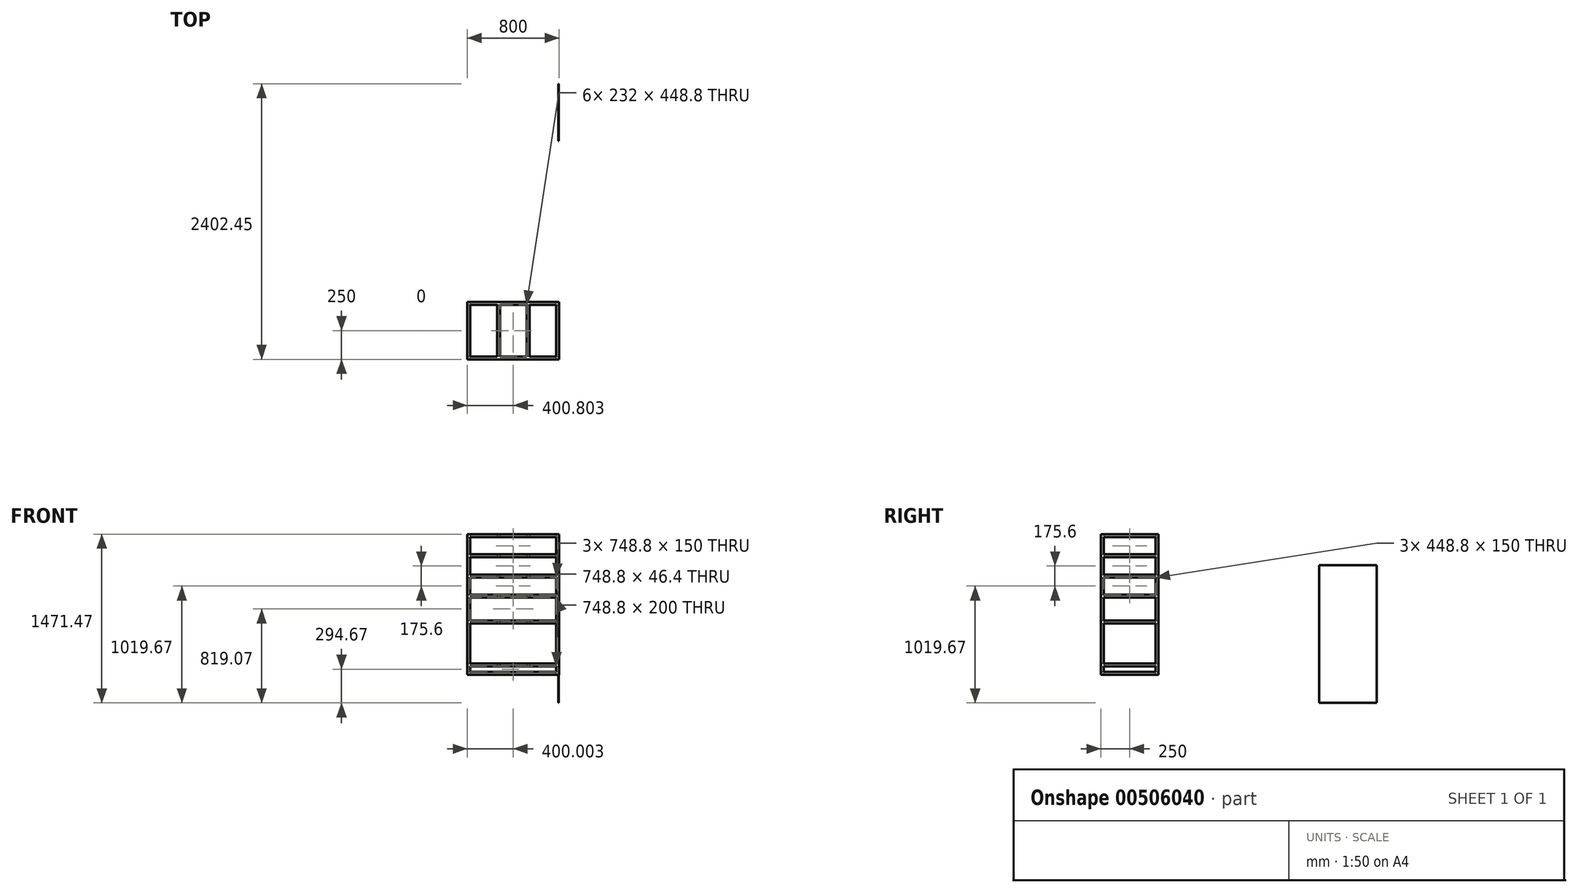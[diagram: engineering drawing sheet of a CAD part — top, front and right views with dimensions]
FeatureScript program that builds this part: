
annotation { "Feature Type Name" : "Feature", "Feature Type Description" : "" }
export const myFeature = defineFeature(function(context is Context, id is Id, definition is map)
    precondition{}
    {
        {
            var Q0;
            Q0=qCreatedBy(makeId("Top.planeOp"),FACE);
            var sketch = newSketch(context, id + "F0", { "sketchPlane" : qUnion([Q0])});
            skLineSegment(sketch, "E0.bottom", {"start": v(-792, -474.11) * mm, "end": v(8, -474.11) * mm});
            skLineSegment(sketch, "E0.top", {"start": v(-792, 25.89) * mm, "end": v(8, 25.89) * mm});
            skLineSegment(sketch, "E0.left", {"start": v(-792, -474.11) * mm, "end": v(-792, 25.89) * mm});
            skLineSegment(sketch, "E0.right", {"start": v(8, -474.11) * mm, "end": v(8, 25.89) * mm});
            skLineSegment(sketch, "E1.0", {"start": v(-766.4, -448.51) * mm, "end": v(-766.4, 0.29) * mm});
            skLineSegment(sketch, "E1.1", {"start": v(-766.4, -448.51) * mm, "end": v(-17.6, -448.51) * mm});
            skLineSegment(sketch, "E1.2", {"start": v(-17.6, -448.51) * mm, "end": v(-17.6, 0.29) * mm});
            skLineSegment(sketch, "E1.3", {"start": v(-766.4, 0.29) * mm, "end": v(-17.6, 0.29) * mm});
            skSolve(sketch);
        }
        {
            var Q0;
            Q0=makeQuery(id+"F0.imprint","IMPRINT",FACE,{"disambiguationData":[TD([[makeQuery(id+"F0.imprint","IMPRINT",EDGE,{"derivedFrom":sQuery(id+"F0.wireOp",EDGE,"E0.bottom")}),1.0]])]});
            extrude(context, id + "F1", {"entities" : qUnion([Q0]), "depth" : 25.6 * mm});
        }
        {
            var Q0;
            Q0=makeQuery(id+"F1.opExtrude","CAP_FACE",FACE,{"disambiguationData":[OSD([sQuery(id+"F0.wireOp",EDGE,"E0.bottom"),sQuery(id+"F0.wireOp",EDGE,"E0.top"),sQuery(id+"F0.wireOp",EDGE,"E0.left"),sQuery(id+"F0.wireOp",EDGE,"E0.right"),sQuery(id+"F0.wireOp",EDGE,"E1.0"),sQuery(id+"F0.wireOp",EDGE,"E1.1"),sQuery(id+"F0.wireOp",EDGE,"E1.2"),sQuery(id+"F0.wireOp",EDGE,"E1.3")])],"isStart":true});
            var sketch = newSketch(context, id + "F2", { "sketchPlane" : qUnion([Q0])});
            skLineSegment(sketch, "E2.bottom", {"start": v(-792, 474.11) * mm, "end": v(-766.4, 474.11) * mm});
            skLineSegment(sketch, "E2.top", {"start": v(-792, 448.51) * mm, "end": v(-766.4, 448.51) * mm});
            skLineSegment(sketch, "E2.left", {"start": v(-792, 474.11) * mm, "end": v(-792, 448.51) * mm});
            skLineSegment(sketch, "E2.right", {"start": v(-766.4, 474.11) * mm, "end": v(-766.4, 448.51) * mm});
            skLineSegment(sketch, "E3.bottom", {"start": v(8, 474.11) * mm, "end": v(-17.6, 474.11) * mm});
            skLineSegment(sketch, "E3.top", {"start": v(8, 448.51) * mm, "end": v(-17.6, 448.51) * mm});
            skLineSegment(sketch, "E3.left", {"start": v(8, 474.11) * mm, "end": v(8, 448.51) * mm});
            skLineSegment(sketch, "E3.right", {"start": v(-17.6, 474.11) * mm, "end": v(-17.6, 448.51) * mm});
            skLineSegment(sketch, "E4.bottom", {"start": v(8, -25.89) * mm, "end": v(-17.6, -25.89) * mm});
            skLineSegment(sketch, "E4.top", {"start": v(8, -0.29) * mm, "end": v(-17.6, -0.29) * mm});
            skLineSegment(sketch, "E4.left", {"start": v(8, -25.89) * mm, "end": v(8, -0.29) * mm});
            skLineSegment(sketch, "E4.right", {"start": v(-17.6, -25.89) * mm, "end": v(-17.6, -0.29) * mm});
            skLineSegment(sketch, "E5.bottom", {"start": v(-792, -25.89) * mm, "end": v(-766.4, -25.89) * mm});
            skLineSegment(sketch, "E5.top", {"start": v(-792, -0.29) * mm, "end": v(-766.4, -0.29) * mm});
            skLineSegment(sketch, "E5.left", {"start": v(-792, -25.89) * mm, "end": v(-792, -0.29) * mm});
            skLineSegment(sketch, "E5.right", {"start": v(-766.4, -25.89) * mm, "end": v(-766.4, -0.29) * mm});
            skSolve(sketch);
        }
        {
            var Q0;
            Q0 = qSketchRegion(id + "F2", true);
            extrude(context, id + "F3", {"entities" : qUnion([Q0]), "operationType" : NewBodyOperationType.ADD, "depth" : (1200) * mm});
        }
        {
            var Q0;
            Q0=makeQuery(id+"F3.opExtrude","SWEPT_FACE",FACE,{"disambiguationData":[OSD([sQuery(id+"F2.wireOp",EDGE,"E2.right")])]});
            var sketch = newSketch(context, id + "F4", { "sketchPlane" : qUnion([Q0])});
            skLineSegment(sketch, "E6.bottom", {"start": v(-474.11, -150) * mm, "end": v(-448.51, -150) * mm});
            skLineSegment(sketch, "E6.top", {"start": v(-474.11, -175.6) * mm, "end": v(-448.51, -175.6) * mm});
            skLineSegment(sketch, "E6.left", {"start": v(-474.11, -150) * mm, "end": v(-474.11, -175.6) * mm});
            skLineSegment(sketch, "E6.right", {"start": v(-448.51, -150) * mm, "end": v(-448.51, -175.6) * mm});
            skLineSegment(sketch, "E7.bottom", {"start": v(-474.11, -325.6) * mm, "end": v(-448.51, -325.6) * mm});
            skLineSegment(sketch, "E7.top", {"start": v(-474.11, -351.2) * mm, "end": v(-448.51, -351.2) * mm});
            skLineSegment(sketch, "E7.left", {"start": v(-474.11, -325.6) * mm, "end": v(-474.11, -351.2) * mm});
            skLineSegment(sketch, "E7.right", {"start": v(-448.51, -325.6) * mm, "end": v(-448.51, -351.2) * mm});
            skLineSegment(sketch, "E8.bottom", {"start": v(-474.11, -501.2) * mm, "end": v(-448.51, -501.2) * mm});
            skLineSegment(sketch, "E8.top", {"start": v(-474.11, -526.8) * mm, "end": v(-448.51, -526.8) * mm});
            skLineSegment(sketch, "E8.left", {"start": v(-474.11, -501.2) * mm, "end": v(-474.11, -526.8) * mm});
            skLineSegment(sketch, "E8.right", {"start": v(-448.51, -501.2) * mm, "end": v(-448.51, -526.8) * mm});
            skLineSegment(sketch, "E9.bottom", {"start": v(-474.11, -726.8) * mm, "end": v(-448.51, -726.8) * mm});
            skLineSegment(sketch, "E9.top", {"start": v(-474.11, -752.4) * mm, "end": v(-448.51, -752.4) * mm});
            skLineSegment(sketch, "E9.left", {"start": v(-474.11, -726.8) * mm, "end": v(-474.11, -752.4) * mm});
            skLineSegment(sketch, "E9.right", {"start": v(-448.51, -726.8) * mm, "end": v(-448.51, -752.4) * mm});
            skLineSegment(sketch, "E10.bottom", {"start": v(-474.11, -1200) * mm, "end": v(-448.51, -1200) * mm});
            skLineSegment(sketch, "E10.top", {"start": v(-474.11, -1174.4) * mm, "end": v(-448.51, -1174.4) * mm});
            skLineSegment(sketch, "E10.left", {"start": v(-474.11, -1200) * mm, "end": v(-474.11, -1174.4) * mm});
            skLineSegment(sketch, "E10.right", {"start": v(-448.51, -1200) * mm, "end": v(-448.51, -1174.4) * mm});
            skLineSegment(sketch, "E11.bottom", {"start": v(-474.11, -1102.4) * mm, "end": v(-448.51, -1102.4) * mm});
            skLineSegment(sketch, "E11.top", {"start": v(-474.11, -1128) * mm, "end": v(-448.51, -1128) * mm});
            skLineSegment(sketch, "E11.left", {"start": v(-474.11, -1102.4) * mm, "end": v(-474.11, -1128) * mm});
            skLineSegment(sketch, "E11.right", {"start": v(-448.51, -1102.4) * mm, "end": v(-448.51, -1128) * mm});
            skLineSegment(sketch, "E12.bottom", {"start": v(0.29, -150) * mm, "end": v(25.89, -150) * mm});
            skLineSegment(sketch, "E12.top", {"start": v(0.29, -175.6) * mm, "end": v(25.89, -175.6) * mm});
            skLineSegment(sketch, "E12.left", {"start": v(0.29, -150) * mm, "end": v(0.29, -175.6) * mm});
            skLineSegment(sketch, "E12.right", {"start": v(25.89, -150) * mm, "end": v(25.89, -175.6) * mm});
            skLineSegment(sketch, "E13.bottom", {"start": v(0.29, -325.6) * mm, "end": v(25.89, -325.6) * mm});
            skLineSegment(sketch, "E13.top", {"start": v(0.29, -351.2) * mm, "end": v(25.89, -351.2) * mm});
            skLineSegment(sketch, "E13.left", {"start": v(0.29, -325.6) * mm, "end": v(0.29, -351.2) * mm});
            skLineSegment(sketch, "E13.right", {"start": v(25.89, -325.6) * mm, "end": v(25.89, -351.2) * mm});
            skLineSegment(sketch, "E14.bottom", {"start": v(0.29, -501.2) * mm, "end": v(25.89, -501.2) * mm});
            skLineSegment(sketch, "E14.top", {"start": v(0.29, -526.8) * mm, "end": v(25.89, -526.8) * mm});
            skLineSegment(sketch, "E14.left", {"start": v(0.29, -501.2) * mm, "end": v(0.29, -526.8) * mm});
            skLineSegment(sketch, "E14.right", {"start": v(25.89, -501.2) * mm, "end": v(25.89, -526.8) * mm});
            skLineSegment(sketch, "E15.bottom", {"start": v(0.29, -726.8) * mm, "end": v(25.89, -726.8) * mm});
            skLineSegment(sketch, "E15.top", {"start": v(0.29, -752.4) * mm, "end": v(25.89, -752.4) * mm});
            skLineSegment(sketch, "E15.left", {"start": v(0.29, -726.8) * mm, "end": v(0.29, -752.4) * mm});
            skLineSegment(sketch, "E15.right", {"start": v(25.89, -726.8) * mm, "end": v(25.89, -752.4) * mm});
            skLineSegment(sketch, "E16.bottom", {"start": v(0.29, -1200) * mm, "end": v(25.89, -1200) * mm});
            skLineSegment(sketch, "E16.top", {"start": v(0.29, -1174.4) * mm, "end": v(25.89, -1174.4) * mm});
            skLineSegment(sketch, "E16.left", {"start": v(0.29, -1200) * mm, "end": v(0.29, -1174.4) * mm});
            skLineSegment(sketch, "E16.right", {"start": v(25.89, -1200) * mm, "end": v(25.89, -1174.4) * mm});
            skLineSegment(sketch, "E17.bottom", {"start": v(0.29, -1102.4) * mm, "end": v(25.89, -1102.4) * mm});
            skLineSegment(sketch, "E17.top", {"start": v(0.29, -1128) * mm, "end": v(25.89, -1128) * mm});
            skLineSegment(sketch, "E17.left", {"start": v(0.29, -1102.4) * mm, "end": v(0.29, -1128) * mm});
            skLineSegment(sketch, "E17.right", {"start": v(25.89, -1102.4) * mm, "end": v(25.89, -1128) * mm});
            skSolve(sketch);
        }
        {
            var Q0;
            Q0 = qSketchRegion(id + "F4", true);
            var Q1;
            Q1=makeQuery(id+"F3.opExtrude","SWEPT_FACE",FACE,{"disambiguationData":[OSD([sQuery(id+"F2.wireOp",EDGE,"E3.right")])]});
            extrude(context, id + "F5", {"entities" : qUnion([Q0]), "operationType" : NewBodyOperationType.ADD, "endBound" : BoundingType.UP_TO_SURFACE, "endBoundEntityFace" : qUnion([Q1]), "depth" : 25 * mm});
        }
        {
            var Q0;
            Q0=makeQuery(id+"F5.boolean.opBoolean","MERGE",FACE,{"derivedFrom":[makeQuery(id+"F3.opExtrude","SWEPT_FACE",FACE,{"disambiguationData":[OSD([sQuery(id+"F2.wireOp",EDGE,"E4.top")])]}),makeQuery(id+"F3.opExtrude","SWEPT_FACE",FACE,{"disambiguationData":[OSD([sQuery(id+"F2.wireOp",EDGE,"E5.top")])]}),makeQuery(id+"F5.opExtrude","SWEPT_FACE",FACE,{"disambiguationData":[OSD([sQuery(id+"F4.wireOp",EDGE,"E12.left")])]}),makeQuery(id+"F5.opExtrude","SWEPT_FACE",FACE,{"disambiguationData":[OSD([sQuery(id+"F4.wireOp",EDGE,"E13.left")])]}),makeQuery(id+"F5.opExtrude","SWEPT_FACE",FACE,{"disambiguationData":[OSD([sQuery(id+"F4.wireOp",EDGE,"E14.left")])]}),makeQuery(id+"F5.opExtrude","SWEPT_FACE",FACE,{"disambiguationData":[OSD([sQuery(id+"F4.wireOp",EDGE,"E15.left")])]}),makeQuery(id+"F5.opExtrude","SWEPT_FACE",FACE,{"disambiguationData":[OSD([sQuery(id+"F4.wireOp",EDGE,"E16.left")])]}),makeQuery(id+"F5.opExtrude","SWEPT_FACE",FACE,{"disambiguationData":[OSD([sQuery(id+"F4.wireOp",EDGE,"E17.left")])]})]});
            var sketch = newSketch(context, id + "F6", { "sketchPlane" : qUnion([Q0])});
            skLineSegment(sketch, "E18.bottom", {"start": v(-792, -150) * mm, "end": v(-766.4, -150) * mm});
            skLineSegment(sketch, "E18.top", {"start": v(-792, -175.6) * mm, "end": v(-766.4, -175.6) * mm});
            skLineSegment(sketch, "E18.left", {"start": v(-792, -150) * mm, "end": v(-792, -175.6) * mm});
            skLineSegment(sketch, "E18.right", {"start": v(-766.4, -150) * mm, "end": v(-766.4, -175.6) * mm});
            skLineSegment(sketch, "E19.bottom", {"start": v(-792, -325.6) * mm, "end": v(-766.4, -325.6) * mm});
            skLineSegment(sketch, "E19.top", {"start": v(-792, -351.2) * mm, "end": v(-766.4, -351.2) * mm});
            skLineSegment(sketch, "E19.left", {"start": v(-792, -325.6) * mm, "end": v(-792, -351.2) * mm});
            skLineSegment(sketch, "E19.right", {"start": v(-766.4, -325.6) * mm, "end": v(-766.4, -351.2) * mm});
            skLineSegment(sketch, "E20.bottom", {"start": v(-792, -501.2) * mm, "end": v(-766.4, -501.2) * mm});
            skLineSegment(sketch, "E20.top", {"start": v(-792, -526.8) * mm, "end": v(-766.4, -526.8) * mm});
            skLineSegment(sketch, "E20.left", {"start": v(-792, -501.2) * mm, "end": v(-792, -526.8) * mm});
            skLineSegment(sketch, "E20.right", {"start": v(-766.4, -501.2) * mm, "end": v(-766.4, -526.8) * mm});
            skLineSegment(sketch, "E21.bottom", {"start": v(-792, -726.8) * mm, "end": v(-766.4, -726.8) * mm});
            skLineSegment(sketch, "E21.top", {"start": v(-792, -752.4) * mm, "end": v(-766.4, -752.4) * mm});
            skLineSegment(sketch, "E21.left", {"start": v(-792, -726.8) * mm, "end": v(-792, -752.4) * mm});
            skLineSegment(sketch, "E21.right", {"start": v(-766.4, -726.8) * mm, "end": v(-766.4, -752.4) * mm});
            skLineSegment(sketch, "E22.bottom", {"start": v(-792, -1200) * mm, "end": v(-766.4, -1200) * mm});
            skLineSegment(sketch, "E22.top", {"start": v(-792, -1174.4) * mm, "end": v(-766.4, -1174.4) * mm});
            skLineSegment(sketch, "E22.left", {"start": v(-792, -1200) * mm, "end": v(-792, -1174.4) * mm});
            skLineSegment(sketch, "E22.right", {"start": v(-766.4, -1200) * mm, "end": v(-766.4, -1174.4) * mm});
            skLineSegment(sketch, "E23.bottom", {"start": v(-792, -1102.4) * mm, "end": v(-766.4, -1102.4) * mm});
            skLineSegment(sketch, "E23.top", {"start": v(-792, -1128) * mm, "end": v(-766.4, -1128) * mm});
            skLineSegment(sketch, "E23.left", {"start": v(-792, -1102.4) * mm, "end": v(-792, -1128) * mm});
            skLineSegment(sketch, "E23.right", {"start": v(-766.4, -1102.4) * mm, "end": v(-766.4, -1128) * mm});
            skLineSegment(sketch, "E24.bottom", {"start": v(-17.6, -150) * mm, "end": v(8, -150) * mm});
            skLineSegment(sketch, "E24.top", {"start": v(-17.6, -175.6) * mm, "end": v(8, -175.6) * mm});
            skLineSegment(sketch, "E24.left", {"start": v(-17.6, -150) * mm, "end": v(-17.6, -175.6) * mm});
            skLineSegment(sketch, "E24.right", {"start": v(8, -150) * mm, "end": v(8, -175.6) * mm});
            skLineSegment(sketch, "E25.bottom", {"start": v(-17.6, -325.6) * mm, "end": v(8, -325.6) * mm});
            skLineSegment(sketch, "E25.top", {"start": v(-17.6, -351.2) * mm, "end": v(8, -351.2) * mm});
            skLineSegment(sketch, "E25.left", {"start": v(-17.6, -325.6) * mm, "end": v(-17.6, -351.2) * mm});
            skLineSegment(sketch, "E25.right", {"start": v(8, -325.6) * mm, "end": v(8, -351.2) * mm});
            skLineSegment(sketch, "E26.bottom", {"start": v(-17.6, -501.2) * mm, "end": v(8, -501.2) * mm});
            skLineSegment(sketch, "E26.top", {"start": v(-17.6, -526.8) * mm, "end": v(8, -526.8) * mm});
            skLineSegment(sketch, "E26.left", {"start": v(-17.6, -501.2) * mm, "end": v(-17.6, -526.8) * mm});
            skLineSegment(sketch, "E26.right", {"start": v(8, -501.2) * mm, "end": v(8, -526.8) * mm});
            skLineSegment(sketch, "E27.bottom", {"start": v(-17.6, -726.8) * mm, "end": v(8, -726.8) * mm});
            skLineSegment(sketch, "E27.top", {"start": v(-17.6, -752.4) * mm, "end": v(8, -752.4) * mm});
            skLineSegment(sketch, "E27.left", {"start": v(-17.6, -726.8) * mm, "end": v(-17.6, -752.4) * mm});
            skLineSegment(sketch, "E27.right", {"start": v(8, -726.8) * mm, "end": v(8, -752.4) * mm});
            skLineSegment(sketch, "E28.bottom", {"start": v(-17.6, -1200) * mm, "end": v(8, -1200) * mm});
            skLineSegment(sketch, "E28.top", {"start": v(-17.6, -1174.4) * mm, "end": v(8, -1174.4) * mm});
            skLineSegment(sketch, "E28.left", {"start": v(-17.6, -1200) * mm, "end": v(-17.6, -1174.4) * mm});
            skLineSegment(sketch, "E28.right", {"start": v(8, -1200) * mm, "end": v(8, -1174.4) * mm});
            skLineSegment(sketch, "E29.bottom", {"start": v(-17.6, -1102.4) * mm, "end": v(8, -1102.4) * mm});
            skLineSegment(sketch, "E29.top", {"start": v(-17.6, -1128) * mm, "end": v(8, -1128) * mm});
            skLineSegment(sketch, "E29.left", {"start": v(-17.6, -1102.4) * mm, "end": v(-17.6, -1128) * mm});
            skLineSegment(sketch, "E29.right", {"start": v(8, -1102.4) * mm, "end": v(8, -1128) * mm});
            skSolve(sketch);
        }
        {
            var Q0;
            Q0 = qSketchRegion(id + "F6", true);
            var Q1;
            Q1=makeQuery(id+"F5.boolean.opBoolean","MERGE",FACE,{"derivedFrom":[makeQuery(id+"F3.opExtrude","SWEPT_FACE",FACE,{"disambiguationData":[OSD([sQuery(id+"F2.wireOp",EDGE,"E2.top")])]}),makeQuery(id+"F3.opExtrude","SWEPT_FACE",FACE,{"disambiguationData":[OSD([sQuery(id+"F2.wireOp",EDGE,"E3.top")])]}),makeQuery(id+"F5.opExtrude","SWEPT_FACE",FACE,{"disambiguationData":[OSD([sQuery(id+"F4.wireOp",EDGE,"E6.right")])]}),makeQuery(id+"F5.opExtrude","SWEPT_FACE",FACE,{"disambiguationData":[OSD([sQuery(id+"F4.wireOp",EDGE,"E7.right")])]}),makeQuery(id+"F5.opExtrude","SWEPT_FACE",FACE,{"disambiguationData":[OSD([sQuery(id+"F4.wireOp",EDGE,"E8.right")])]}),makeQuery(id+"F5.opExtrude","SWEPT_FACE",FACE,{"disambiguationData":[OSD([sQuery(id+"F4.wireOp",EDGE,"E9.right")])]}),makeQuery(id+"F5.opExtrude","SWEPT_FACE",FACE,{"disambiguationData":[OSD([sQuery(id+"F4.wireOp",EDGE,"E10.right")])]}),makeQuery(id+"F5.opExtrude","SWEPT_FACE",FACE,{"disambiguationData":[OSD([sQuery(id+"F4.wireOp",EDGE,"E11.right")])]})]});
            extrude(context, id + "F7", {"entities" : qUnion([Q0]), "operationType" : NewBodyOperationType.ADD, "endBound" : BoundingType.UP_TO_SURFACE, "endBoundEntityFace" : qUnion([Q1]), "depth" : 25 * mm});
        }
        {
            var Q0;
            Q0=makeQuery(id+"F1.opExtrude","SWEPT_FACE",FACE,{"disambiguationData":[OSD([sQuery(id+"F0.wireOp",EDGE,"E1.1")])]});
            var sketch = newSketch(context, id + "F8", { "sketchPlane" : qUnion([Q0])});
            skLineSegment(sketch, "E30.bottom", {"start": v(249.6, 25.6) * mm, "end": v(275.2, 25.6) * mm});
            skLineSegment(sketch, "E30.top", {"start": v(249.6, 0) * mm, "end": v(275.2, 0) * mm});
            skLineSegment(sketch, "E30.left", {"start": v(249.6, 25.6) * mm, "end": v(249.6, 0) * mm});
            skLineSegment(sketch, "E30.right", {"start": v(275.2, 25.6) * mm, "end": v(275.2, 0) * mm});
            skLineSegment(sketch, "E31.bottom", {"start": v(507.2, 25.6) * mm, "end": v(532.8, 25.6) * mm});
            skLineSegment(sketch, "E31.top", {"start": v(507.2, 0) * mm, "end": v(532.8, 0) * mm});
            skLineSegment(sketch, "E31.left", {"start": v(507.2, 25.6) * mm, "end": v(507.2, 0) * mm});
            skLineSegment(sketch, "E31.right", {"start": v(532.8, 25.6) * mm, "end": v(532.8, 0) * mm});
            skLineSegment(sketch, "E32.bottom", {"start": v(249.6, -150) * mm, "end": v(275.2, -150) * mm});
            skLineSegment(sketch, "E32.top", {"start": v(249.6, -175.6) * mm, "end": v(275.2, -175.6) * mm});
            skLineSegment(sketch, "E32.left", {"start": v(249.6, -150) * mm, "end": v(249.6, -175.6) * mm});
            skLineSegment(sketch, "E32.right", {"start": v(275.2, -150) * mm, "end": v(275.2, -175.6) * mm});
            skLineSegment(sketch, "E33.bottom", {"start": v(507.2, -175.6) * mm, "end": v(532.8, -175.6) * mm});
            skLineSegment(sketch, "E33.top", {"start": v(507.2, -150) * mm, "end": v(532.8, -150) * mm});
            skLineSegment(sketch, "E33.left", {"start": v(507.2, -150) * mm, "end": v(507.2, -175.6) * mm});
            skLineSegment(sketch, "E33.right", {"start": v(532.8, -150) * mm, "end": v(532.8, -175.6) * mm});
            skLineSegment(sketch, "E34.bottom", {"start": v(249.6, -325.6) * mm, "end": v(275.2, -325.6) * mm});
            skLineSegment(sketch, "E34.top", {"start": v(249.6, -351.2) * mm, "end": v(275.2, -351.2) * mm});
            skLineSegment(sketch, "E34.left", {"start": v(249.6, -325.6) * mm, "end": v(249.6, -351.2) * mm});
            skLineSegment(sketch, "E34.right", {"start": v(275.2, -325.6) * mm, "end": v(275.2, -351.2) * mm});
            skLineSegment(sketch, "E35.bottom", {"start": v(507.2, -351.2) * mm, "end": v(532.8, -351.2) * mm});
            skLineSegment(sketch, "E35.top", {"start": v(507.2, -325.6) * mm, "end": v(532.8, -325.6) * mm});
            skLineSegment(sketch, "E35.left", {"start": v(507.2, -325.6) * mm, "end": v(507.2, -351.2) * mm});
            skLineSegment(sketch, "E35.right", {"start": v(532.8, -325.6) * mm, "end": v(532.8, -351.2) * mm});
            skLineSegment(sketch, "E36.bottom", {"start": v(249.6, -501.2) * mm, "end": v(275.2, -501.2) * mm});
            skLineSegment(sketch, "E36.top", {"start": v(249.6, -526.8) * mm, "end": v(275.2, -526.8) * mm});
            skLineSegment(sketch, "E36.left", {"start": v(249.6, -501.2) * mm, "end": v(249.6, -526.8) * mm});
            skLineSegment(sketch, "E36.right", {"start": v(275.2, -501.2) * mm, "end": v(275.2, -526.8) * mm});
            skLineSegment(sketch, "E37.bottom", {"start": v(507.2, -526.8) * mm, "end": v(532.8, -526.8) * mm});
            skLineSegment(sketch, "E37.top", {"start": v(507.2, -501.2) * mm, "end": v(532.8, -501.2) * mm});
            skLineSegment(sketch, "E37.left", {"start": v(507.2, -501.2) * mm, "end": v(507.2, -526.8) * mm});
            skLineSegment(sketch, "E37.right", {"start": v(532.8, -501.2) * mm, "end": v(532.8, -526.8) * mm});
            skLineSegment(sketch, "E38.bottom", {"start": v(249.6, -726.8) * mm, "end": v(275.2, -726.8) * mm});
            skLineSegment(sketch, "E38.top", {"start": v(249.6, -752.4) * mm, "end": v(275.2, -752.4) * mm});
            skLineSegment(sketch, "E38.left", {"start": v(249.6, -726.8) * mm, "end": v(249.6, -752.4) * mm});
            skLineSegment(sketch, "E38.right", {"start": v(275.2, -726.8) * mm, "end": v(275.2, -752.4) * mm});
            skLineSegment(sketch, "E39.bottom", {"start": v(507.2, -752.4) * mm, "end": v(532.8, -752.4) * mm});
            skLineSegment(sketch, "E39.top", {"start": v(507.2, -726.8) * mm, "end": v(532.8, -726.8) * mm});
            skLineSegment(sketch, "E39.left", {"start": v(507.2, -726.8) * mm, "end": v(507.2, -752.4) * mm});
            skLineSegment(sketch, "E39.right", {"start": v(532.8, -726.8) * mm, "end": v(532.8, -752.4) * mm});
            skLineSegment(sketch, "E40.bottom", {"start": v(249.6, -1102.4) * mm, "end": v(275.2, -1102.4) * mm});
            skLineSegment(sketch, "E40.top", {"start": v(249.6, -1128) * mm, "end": v(275.2, -1128) * mm});
            skLineSegment(sketch, "E40.left", {"start": v(249.6, -1102.4) * mm, "end": v(249.6, -1128) * mm});
            skLineSegment(sketch, "E40.right", {"start": v(275.2, -1102.4) * mm, "end": v(275.2, -1128) * mm});
            skLineSegment(sketch, "E41.bottom", {"start": v(507.2, -1128) * mm, "end": v(532.8, -1128) * mm});
            skLineSegment(sketch, "E41.top", {"start": v(507.2, -1102.4) * mm, "end": v(532.8, -1102.4) * mm});
            skLineSegment(sketch, "E41.left", {"start": v(507.2, -1102.4) * mm, "end": v(507.2, -1128) * mm});
            skLineSegment(sketch, "E41.right", {"start": v(532.8, -1102.4) * mm, "end": v(532.8, -1128) * mm});
            skSolve(sketch);
        }
        {
            var Q0;
            Q0 = qSketchRegion(id + "F8", true);
            var Q1;
            Q1=makeQuery(id+"F1.opExtrude","SWEPT_FACE",FACE,{"disambiguationData":[OSD([sQuery(id+"F0.wireOp",EDGE,"E1.3")])]});
            extrude(context, id + "F9", {"entities" : qUnion([Q0]), "operationType" : NewBodyOperationType.ADD, "endBound" : BoundingType.UP_TO_SURFACE, "endBoundEntityFace" : qUnion([Q1]), "depth" : 25 * mm});
        }
        {
            var Q0;
            Q0=qCreatedBy(makeId("Right.planeOp"),FACE);
            var sketch = newSketch(context, id + "F10", { "sketchPlane" : qUnion([Q0])});
            skLineSegment(sketch, "E42.bottom", {"start": v(1428.34, -245.87) * mm, "end": v(1928.34, -245.87) * mm});
            skLineSegment(sketch, "E42.top", {"start": v(1428.34, -1445.87) * mm, "end": v(1928.34, -1445.87) * mm});
            skLineSegment(sketch, "E42.left", {"start": v(1428.34, -245.87) * mm, "end": v(1428.34, -1445.87) * mm});
            skLineSegment(sketch, "E42.right", {"start": v(1928.34, -245.87) * mm, "end": v(1928.34, -1445.87) * mm});
            skSolve(sketch);
        }
        {
            var Q0;
            Q0 = qSketchRegion(id + "F10", true);
            extrude(context, id + "F11", {"entities" : qUnion([Q0]), "depth" : 5 * mm});
        }
    });
